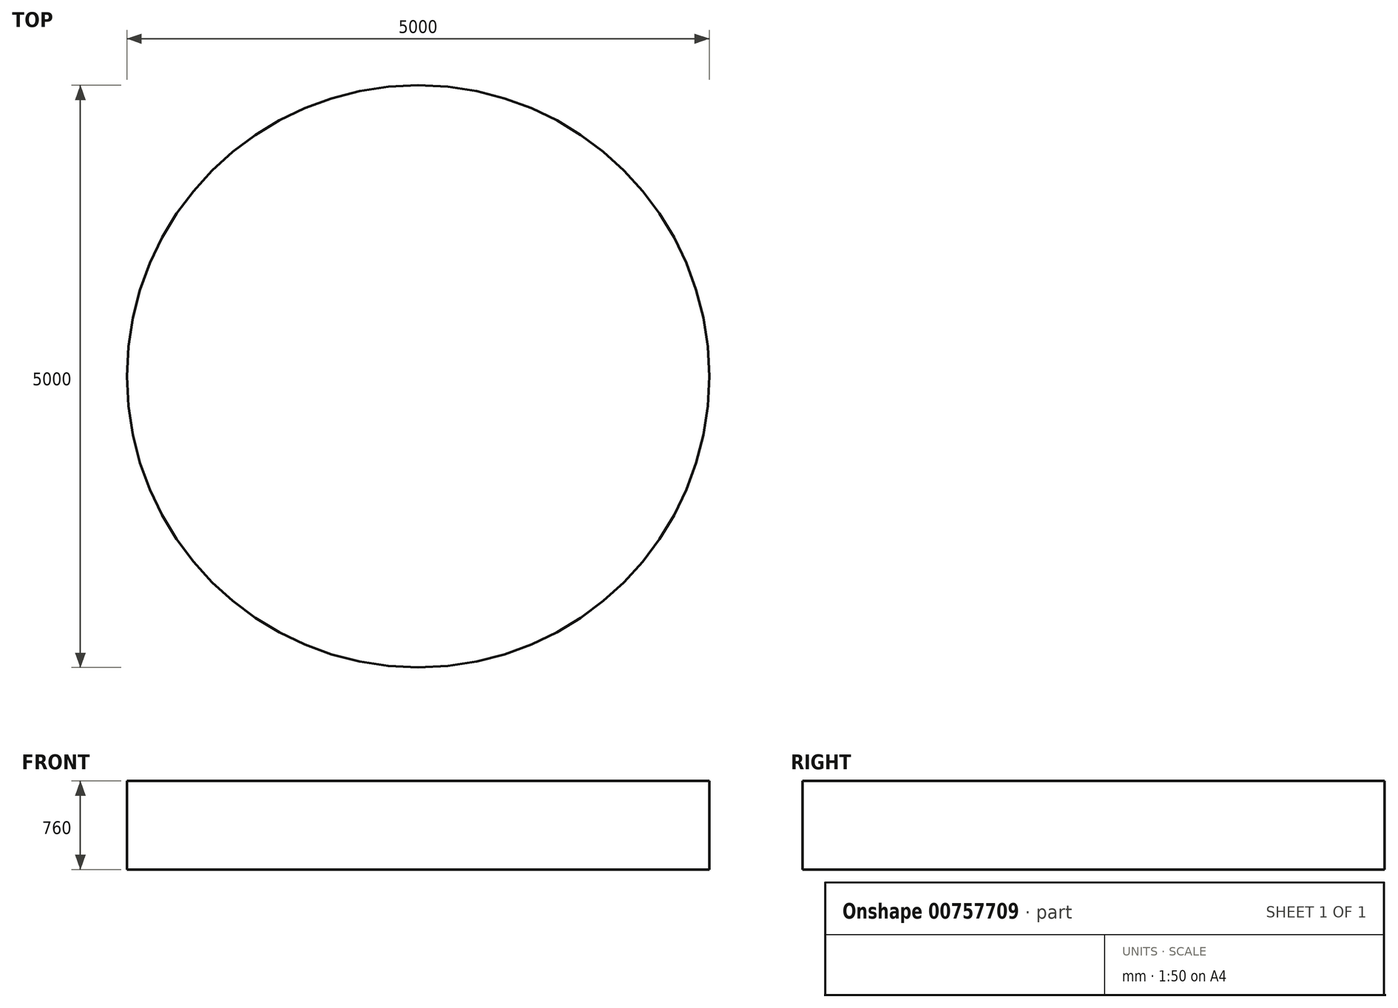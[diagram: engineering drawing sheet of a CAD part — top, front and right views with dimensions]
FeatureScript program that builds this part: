
annotation { "Feature Type Name" : "Feature", "Feature Type Description" : "" }
export const myFeature = defineFeature(function(context is Context, id is Id, definition is map)
    precondition{}
    {
        {
            var Q0;
            Q0=qCreatedBy(makeId("Top.planeOp"),FACE);
            var sketch = newSketch(context, id + "F0", { "sketchPlane" : qUnion([Q0])});
            skCircle(sketch, "E0", {"center": v(14.97, 19.69) * mm, "radius": 2500 * mm});
            skSolve(sketch);
        }
        {
            var Q0;
            Q0 = qSketchRegion(id + "F0", true);
            extrude(context, id + "F1", {"entities" : qUnion([Q0]), "oppositeDirection" : true, "depth" : 760 * mm, "offsetDistance" : 25 * mm});
        }
    });
